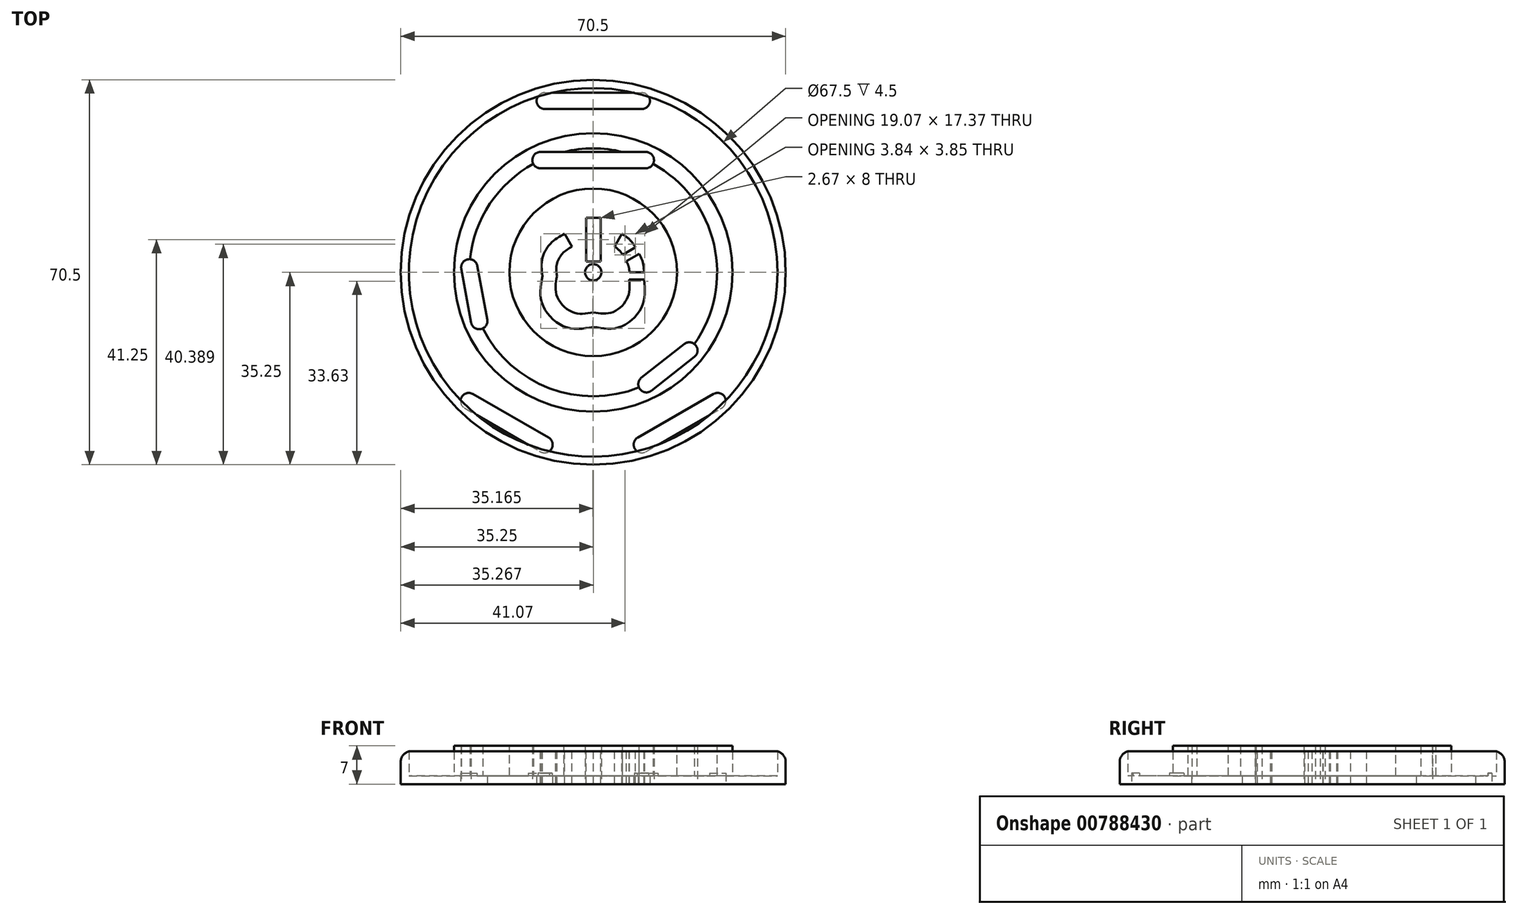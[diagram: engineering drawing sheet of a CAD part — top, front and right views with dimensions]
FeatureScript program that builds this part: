
annotation { "Feature Type Name" : "Feature", "Feature Type Description" : "" }
export const myFeature = defineFeature(function(context is Context, id is Id, definition is map)
    precondition{}
    {
        {
            var Q0;
            Q0=qCreatedBy(makeId("Top.planeOp"),FACE);
            var sketch = newSketch(context, id + "F0", { "sketchPlane" : qUnion([Q0])});
            skCircle(sketch, "E0", {"center": v(0, 0) * mm, "radius": 32.8 * mm});
            skSolve(sketch);
        }
        {
            var Q0;
            Q0=qCreatedBy(makeId("Top.planeOp"),FACE);
            var sketch = newSketch(context, id + "F1", { "sketchPlane" : qUnion([Q0])});
            skCircle(sketch, "E1", {"center": v(0, 0) * mm, "radius": 26.15 * mm});
            skSolve(sketch);
        }
        {
            var Q0;
            Q0=qCreatedBy(makeId("Top.planeOp"),FACE);
            var sketch = newSketch(context, id + "F2", { "sketchPlane" : qUnion([Q0])});
            skCircle(sketch, "E2", {"center": v(0, 0) * mm, "radius": 35.25 * mm});
            skSolve(sketch);
        }
        {
            var Q0;
            Q0=qCreatedBy(makeId("Top.planeOp"),FACE);
            var sketch = newSketch(context, id + "F3", { "sketchPlane" : qUnion([Q0])});
            skCircle(sketch, "E3", {"center": v(0, 0) * mm, "radius": 25.5 * mm});
            skSolve(sketch);
        }
        {
            var Q0;
            Q0=qSketchRegion(id+"F2",true);
            extrude(context, id + "F4", {"entities" : qUnion([Q0]), "depth" : 6 * mm, "offsetDistance" : 25 * mm});
        }
        {
            var Q0;
            Q0=makeQuery(id+"F4.opExtrude","CAP_FACE",FACE,{"disambiguationData":[OSD([sQuery(id+"F2.wireOp",EDGE,"E2")])],"isStart":false});
            shell(context, id + "F5", {"entities" : qUnion([Q0]), "thickness" : 1.5 * mm});
        }
        {
            var Q0;
            Q0=qSketchRegion(id+"F3",true);
            extrude(context, id + "F6", {"entities" : qUnion([Q0]), "operationType" : NewBodyOperationType.ADD, "depth" : 7 * mm, "offsetDistance" : 25 * mm});
        }
        {
            var Q0;
            Q0=makeQuery(id+"F6.opExtrude","CAP_FACE",FACE,{"disambiguationData":[OSD([sQuery(id+"F3.wireOp",EDGE,"E3")])],"isStart":false});
            var sketch = newSketch(context, id + "F7", { "sketchPlane" : qUnion([Q0])});
            skCircle(sketch, "E4", {"center": v(0, 0) * mm, "radius": 22.7 * mm});
            skSolve(sketch);
        }
        {
            var Q0;
            Q0=makeQuery(id+"F7.imprint","IMPRINT",FACE,{"disambiguationData":[TD([[makeQuery(id+"F7.imprint","IMPRINT",EDGE,{"derivedFrom":sQuery(id+"F7.wireOp",EDGE,"E4")}),1.0]])]});
            var sketch = newSketch(context, id + "F8", { "sketchPlane" : qUnion([Q0])});
            skCircle(sketch, "E5", {"center": v(0, 0) * mm, "radius": 15.35 * mm});
            skSolve(sketch);
        }
        {
            var Q0;
            Q0=makeQuery(id+"F8.imprint","IMPRINT",FACE,{"disambiguationData":[TD([[makeQuery(id+"F8.imprint","IMPRINT",EDGE,{"derivedFrom":sQuery(id+"F8.wireOp",EDGE,"E5")}),-1.0]])]});
            extrude(context, id + "F9", {"entities" : qUnion([Q0]), "operationType" : NewBodyOperationType.REMOVE, "oppositeDirection" : true, "depth" : 5.5 * mm, "offsetDistance" : 25 * mm});
        }
        {
            var Q0;
            Q0=makeQuery(id+"F4.opExtrude","CAP_EDGE",EDGE,{"disambiguationData":[OSD([sQuery(id+"F2.wireOp",EDGE,"E2")])],"isStart":false});
            var Q1;
            Q1=makeQuery(id+"F9.boolean.opBoolean","COPY",EDGE,{"derivedFrom":makeQuery(id+"F9.opExtrude","CAP_EDGE",EDGE,{"disambiguationData":[OSD([sQuery(id+"F8.wireOp",EDGE,"E5")])],"isStart":true})});
            fillet(context, id + "F10", {"entities" : qUnion([Q0, Q1]), "radius" : 2 * mm, "tangentPropagation" : true, "allowEdgeOverflow" : false});
        }
        {
            var Q0;
            Q0=makeQuery(id+"F7.imprint","IMPRINT",FACE,{"disambiguationData":[TD([[makeQuery(id+"F7.imprint","IMPRINT",EDGE,{"derivedFrom":sQuery(id+"F7.wireOp",EDGE,"E4")}),1.0]])]});
            var sketch = newSketch(context, id + "F11", { "sketchPlane" : qUnion([Q0])});
            skFitSpline(sketch, "E6", {"points": [v(9.3, 0) * mm, v(9.22, 1.21) * mm, v(8.9, 2.36) * mm, v(8.4, 3.4) * mm]});
            skLineSegment(sketch, "E7", {"start": v(6.64, 0) * mm, "end": v(9.3, 0) * mm});
            skLineSegment(sketch, "E8", {"start": v(9.3, 0) * mm, "end": v(6.64, 0) * mm});
            skFitSpline(sketch, "E9", {"points": [v(6.08, 2.06) * mm, v(6.37, 1.42) * mm, v(6.57, 0.73) * mm, v(6.64, 0) * mm]});
            skLineSegment(sketch, "E10", {"start": v(8.4, 3.4) * mm, "end": v(6.08, 2.06) * mm});
            skLineSegment(sketch, "E11", {"start": v(6.08, 2.06) * mm, "end": v(8.4, 3.4) * mm});
            skFitSpline(sketch, "E12", {"points": [v(7.74, 4.56) * mm, v(7.07, 5.54) * mm, v(6.23, 6.4) * mm, v(5.25, 7.06) * mm]});
            skLineSegment(sketch, "E13", {"start": v(5.4, 3.22) * mm, "end": v(7.74, 4.56) * mm});
            skLineSegment(sketch, "E14", {"start": v(7.74, 4.56) * mm, "end": v(5.4, 3.22) * mm});
            skFitSpline(sketch, "E15", {"points": [v(3.9, 4.73) * mm, v(4.48, 4.3) * mm, v(4.99, 3.8) * mm, v(5.4, 3.22) * mm]});
            skLineSegment(sketch, "E16", {"start": v(5.25, 7.06) * mm, "end": v(3.9, 4.73) * mm});
            skLineSegment(sketch, "E17", {"start": v(3.9, 4.73) * mm, "end": v(5.25, 7.06) * mm});
            skFitSpline(sketch, "E18", {"points": [v(6.62, -1.33) * mm, v(6.28, -4.7) * mm, v(3.46, -7.33) * mm, v(0.02, -7.33) * mm]});
            skFitSpline(sketch, "E19", {"points": [v(0.02, -7.33) * mm, v(-3.66, -7.33) * mm, v(-6.65, -4.34) * mm, v(-6.65, -0.67) * mm]});
            skFitSpline(sketch, "E20", {"points": [v(-6.65, -0.67) * mm, v(-6.65, 1.56) * mm, v(-5.55, 3.52) * mm, v(-3.87, 4.73) * mm]});
            skFitSpline(sketch, "E21", {"points": [v(-5.21, 7.06) * mm, v(-7.69, 5.38) * mm, v(-9.32, 2.55) * mm, v(-9.32, -0.67) * mm]});
            skFitSpline(sketch, "E22", {"points": [v(-9.32, -0.67) * mm, v(-9.32, -5.82) * mm, v(-5.14, -10) * mm, v(0.02, -10) * mm]});
            skFitSpline(sketch, "E23", {"points": [v(0.02, -10) * mm, v(4.95, -10) * mm, v(8.97, -6.18) * mm, v(9.32, -1.33) * mm]});
            skLineSegment(sketch, "E24", {"start": v(-3.87, 4.73) * mm, "end": v(-5.21, 7.06) * mm});
            skLineSegment(sketch, "E25", {"start": v(-5.21, 7.06) * mm, "end": v(-3.87, 4.73) * mm});
            skLineSegment(sketch, "E26", {"start": v(9.32, -1.33) * mm, "end": v(6.62, -1.33) * mm});
            skLineSegment(sketch, "E27", {"start": v(6.62, -1.33) * mm, "end": v(9.32, -1.33) * mm});
            skLineSegment(sketch, "E28", {"start": v(-1.32, 10) * mm, "end": v(1.35, 10) * mm});
            skLineSegment(sketch, "E29", {"start": v(1.35, 10) * mm, "end": v(1.35, 2) * mm});
            skLineSegment(sketch, "E30", {"start": v(1.35, 2) * mm, "end": v(-1.32, 2) * mm});
            skLineSegment(sketch, "E31", {"start": v(-1.32, 2) * mm, "end": v(-1.32, 10) * mm});
            skSolve(sketch);
        }
        {
            var Q0;
            Q0=qSketchRegion(id+"F11",true);
            extrude(context, id + "F12", {"entities" : qUnion([Q0]), "operationType" : NewBodyOperationType.REMOVE, "oppositeDirection" : true, "depth" : 8 * mm, "offsetDistance" : 25 * mm});
        }
        {
            var Q0;
            Q0=qCreatedBy(makeId("Top.planeOp"),FACE);
            var sketch = newSketch(context, id + "F13", { "sketchPlane" : qUnion([Q0])});
            skLineSegment(sketch, "E32", {"start": v(0, 0) * mm, "end": v(0, 32.8) * mm});
            skCircle(sketch, "E33", {"center": v(8.9, 31.4) * mm, "radius": 1.5 * mm});
            skCircle(sketch, "E34", {"center": v(-8.86, 31.4) * mm, "radius": 1.5 * mm});
            skLineSegment(sketch, "E35.top", {"start": v(-8.86, 32.9) * mm, "end": v(8.9, 32.9) * mm});
            skLineSegment(sketch, "E35.left", {"start": v(-8.86, 31.4) * mm, "end": v(-8.86, 32.9) * mm});
            skLineSegment(sketch, "E35.right", {"start": v(8.9, 31.35) * mm, "end": v(8.9, 32.9) * mm});
            skLineSegment(sketch, "E36.top", {"start": v(-8.86, 29.9) * mm, "end": v(8.9, 29.9) * mm});
            skLineSegment(sketch, "E36.left", {"start": v(-8.86, 31.4) * mm, "end": v(-8.86, 29.9) * mm});
            skLineSegment(sketch, "E36.right", {"start": v(8.9, 31.35) * mm, "end": v(8.9, 29.9) * mm});
            skSolve(sketch);
        }
        {
            var Q0;
            Q0=qSketchRegion(id+"F13",true);
            extrude(context, id + "F14", {"entities" : qUnion([Q0]), "operationType" : NewBodyOperationType.REMOVE, "depth" : 2 * mm, "offsetDistance" : 25 * mm});
        }
        {
            var Q0;
            Q0=qCreatedBy(makeId("Top.planeOp"),FACE);
            var sketch = newSketch(context, id + "F15", { "sketchPlane" : qUnion([Q0])});
            skLineSegment(sketch, "E37", {"start": v(0, 0) * mm, "end": v(0, -32.8) * mm});
            skLineSegment(sketch, "E38", {"start": v(0, -32.8) * mm, "end": v(8.91, -31.57) * mm});
            skLineSegment(sketch, "E39", {"start": v(0, -32.8) * mm, "end": v(-8.91, -31.57) * mm});
            skLineSegment(sketch, "E40", {"start": v(8.91, -31.57) * mm, "end": v(22.79, -23.6) * mm});
            skLineSegment(sketch, "E41", {"start": v(-8.91, -31.57) * mm, "end": v(-22.79, -23.6) * mm});
            skCircle(sketch, "E42", {"center": v(-22.79, -23.6) * mm, "radius": 1.5 * mm});
            skCircle(sketch, "E43", {"center": v(-8.91, -31.57) * mm, "radius": 1.5 * mm});
            skCircle(sketch, "E44", {"center": v(8.91, -31.57) * mm, "radius": 1.5 * mm});
            skCircle(sketch, "E45", {"center": v(22.79, -23.6) * mm, "radius": 1.5 * mm});
            skLineSegment(sketch, "E46", {"start": v(9.66, -32.87) * mm, "end": v(23.53, -24.9) * mm});
            skLineSegment(sketch, "E47", {"start": v(8.17, -30.26) * mm, "end": v(22.04, -22.3) * mm});
            skLineSegment(sketch, "E48", {"start": v(-23.53, -24.9) * mm, "end": v(-9.66, -32.87) * mm});
            skLineSegment(sketch, "E49", {"start": v(-22.04, -22.3) * mm, "end": v(-8.17, -30.26) * mm});
            skSolve(sketch);
        }
        {
            var Q0;
            Q0=qSketchRegion(id+"F15",true);
            extrude(context, id + "F16", {"entities" : qUnion([Q0]), "operationType" : NewBodyOperationType.REMOVE, "depth" : 2 * mm, "offsetDistance" : 25 * mm});
        }
        {
            var Q0;
            Q0=qCreatedBy(makeId("Top.planeOp"),FACE);
            var sketch = newSketch(context, id + "F17", { "sketchPlane" : qUnion([Q0])});
            skLineSegment(sketch, "E50", {"start": v(0, 0) * mm, "end": v(0, 22.7) * mm});
            skCircle(sketch, "E51", {"center": v(-9.63, 20.55) * mm, "radius": 1.5 * mm});
            skCircle(sketch, "E52", {"center": v(9.63, 20.55) * mm, "radius": 1.5 * mm});
            skLineSegment(sketch, "E53.bottom", {"start": v(-9.63, 20.55) * mm, "end": v(9.62, 20.55) * mm});
            skLineSegment(sketch, "E53.top", {"start": v(-9.63, 19.05) * mm, "end": v(9.62, 19.05) * mm});
            skLineSegment(sketch, "E53.left", {"start": v(-9.63, 20.55) * mm, "end": v(-9.63, 19.05) * mm});
            skLineSegment(sketch, "E53.right", {"start": v(9.62, 20.55) * mm, "end": v(9.62, 19.05) * mm});
            skLineSegment(sketch, "E54.top", {"start": v(-9.63, 22.05) * mm, "end": v(9.62, 22.05) * mm});
            skLineSegment(sketch, "E54.left", {"start": v(-9.63, 20.55) * mm, "end": v(-9.63, 22.05) * mm});
            skLineSegment(sketch, "E54.right", {"start": v(9.62, 20.55) * mm, "end": v(9.62, 22.05) * mm});
            skSolve(sketch);
        }
        {
            var Q0;
            Q0=qCreatedBy(makeId("Top.planeOp"),FACE);
            var sketch = newSketch(context, id + "F18", { "sketchPlane" : qUnion([Q0])});
            skLineSegment(sketch, "E55", {"start": v(0, 0) * mm, "end": v(0, -22.7) * mm});
            skLineSegment(sketch, "E56", {"start": v(0, -22.7) * mm, "end": v(9.75, -20.5) * mm});
            skLineSegment(sketch, "E57", {"start": v(9.75, -20.5) * mm, "end": v(17.62, -14.32) * mm});
            skLineSegment(sketch, "E58", {"start": v(0, -22.7) * mm, "end": v(-20.87, -8.93) * mm});
            skLineSegment(sketch, "E59", {"start": v(-20.87, -8.93) * mm, "end": v(-22.68, 0.9) * mm});
            skCircle(sketch, "E60", {"center": v(-22.68, 0.9) * mm, "radius": 1.5 * mm});
            skCircle(sketch, "E61", {"center": v(-20.87, -8.93) * mm, "radius": 1.5 * mm});
            skCircle(sketch, "E62", {"center": v(9.75, -20.5) * mm, "radius": 1.5 * mm});
            skCircle(sketch, "E63", {"center": v(17.62, -14.32) * mm, "radius": 1.5 * mm});
            skLineSegment(sketch, "E64", {"start": v(10.68, -21.68) * mm, "end": v(18.54, -15.5) * mm});
            skLineSegment(sketch, "E65", {"start": v(8.83, -19.32) * mm, "end": v(16.69, -13.14) * mm});
            skLineSegment(sketch, "E66", {"start": v(-19.4, -8.66) * mm, "end": v(-21.2, 1.17) * mm});
            skLineSegment(sketch, "E67", {"start": v(-22.34, -9.23) * mm, "end": v(-24.15, 0.6) * mm});
            skSolve(sketch);
        }
        {
            var Q0;
            Q0=qSketchRegion(id+"F17",true);
            var Q1;
            Q1=qSketchRegion(id+"F18",true);
            extrude(context, id + "F19", {"entities" : qUnion([Q0, Q1]), "operationType" : NewBodyOperationType.REMOVE, "endBound" : BoundingType.THROUGH_ALL, "depth" : 2 * mm, "offsetDistance" : 25 * mm});
        }
        {
            var Q0;
            Q0=qCreatedBy(makeId("Top.planeOp"),FACE);
            var sketch = newSketch(context, id + "F20", { "sketchPlane" : qUnion([Q0])});
            skCircle(sketch, "E68", {"center": v(0, 0) * mm, "radius": 1.5 * mm});
            skSolve(sketch);
        }
        {
            var Q0;
            Q0=qSketchRegion(id+"F20",true);
            extrude(context, id + "F21", {"entities" : qUnion([Q0]), "operationType" : NewBodyOperationType.REMOVE, "depth" : 8 * mm, "offsetDistance" : 25 * mm});
        }
    });
